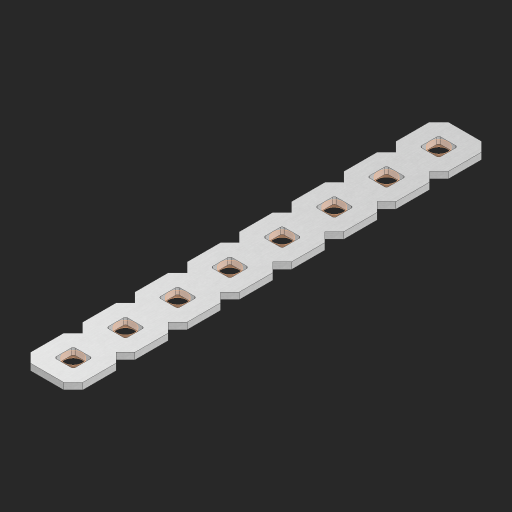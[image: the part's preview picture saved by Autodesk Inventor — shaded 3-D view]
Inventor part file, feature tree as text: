
AUTODESK INVENTOR PART (.ipt)
format: ipt  version: 2023 (Build 270158000, 158)  size: 352,768 bytes
history: native  units: in
note: dims shown in document units (in); Inventor stores cm internally (conversion verified against a paired STEP export)
features: other x9, extrude x7, sketch x2, pattern_linear x1
ambient origin geometry x8: Origin, YZ Plane, XZ Plane, XY Plane, X Axis, Y Axis, Z Axis, Center Point
bodies: Solid1 (feature_tree), Body (feature_tree)
feature tree (19):
  pattern_linear  "Rectangular Pattern1"  Spacing1=0.09in  [1 undecoded]
  sketch  "Sketch1"  dims[d1=0.5in]
  sketch  "Sketch2"  dims[d2=0.182in d3=0.09in d4=0.09in d5=0.09in d6=0.09in d7=0.09in d8=0.09in d9=0.09in d10=0.09in d11=0.02in d13=0.0in d14=0.172in d15=0.0625in d16=0.0in d19=0.5in d22=0.5in]
  other  "Srf1"
  other  "Srf126"
  other  "Srf127"
  other  "Srf128"
  other  "Srf129"
  other  "Srf130"
  other  "Srf131"
  other  "Srf250"
  other  "Circle"
  extrude  "ExtrusionSrf126"  Depth=0.09in
  extrude  "ExtrusionSrf127"  Depth=0.09in
  extrude  "ExtrusionSrf128"  Depth=0.09in
  extrude  "ExtrusionSrf129"  Depth=0.09in
  extrude  "ExtrusionSrf130"  Depth=0.09in
  extrude  "ExtrusionSrf131"  Depth=0.09in
  extrude  "ExtrusionSrf250"  Depth=0.09in
note: 1 required parameter value undecoded (feature->parameter linkage not recoverable at this tier; creation-order binding heuristic only, values carry confidence <= 0.55)
